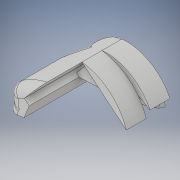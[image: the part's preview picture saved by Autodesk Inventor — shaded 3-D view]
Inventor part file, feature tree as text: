
AUTODESK INVENTOR PART (.ipt)
format: ipt  version: 2017 (Build 210142000, 142)  size: 672,768 bytes
history: native  units: mm
features: sketch x24, extrude x20, fillet x6, plane x5, other x3, boolean_combine x1, revolve x1, sweep x1
ambient origin geometry x8: Origin, YZ Plane, XZ Plane, XY Plane, X Axis, Y Axis, Z Axis, Center Point
bodies: Solid1 (feature_tree), Solid2 (feature_tree), Solid3 (feature_tree), Solid4 (feature_tree), Solid5 (feature_tree)
feature tree (61):
  extrude  "Extrusion1"  Depth=35.0mm
  plane  "Work Plane1"
  extrude  "Extrusion2"  Depth=33.005mm
  extrude  "Extrusion3"  TaperAngle=0.0deg  [1 undecoded]
  plane  "Work Plane2"
  extrude  "Extrusion4"  Depth=20.0mm
  other  "Work Axis1"
  extrude  "Extrusion5"  Depth=10.0mm
  sketch  "Sketch6"  dims[d12=48.556624mm d13=20.0mm d14=0.0mm]
  boolean_combine  "Combine1"
  extrude  "Extrusion6"  Depth=20.0mm TaperAngle=0.0deg
  extrude  "Extrusion7"  Depth=20.0mm TaperAngle=0.0deg
  other  "Work Axis2"
  fillet  "Fillet1"  Radius=53.287466mm
  revolve  "Revolution1"  [1 undecoded]
  extrude  "Extrusion8"  Depth=20.0mm
  sketch  "Sketch10"  dims[d25=7.433428mm d26=13.25mm d27=0.0mm]
  plane  "Work Plane3"
  sweep  "Sweep1"
  extrude  "Extrusion9"  TaperAngle=90.0deg  [1 undecoded]
  fillet  "Fillet2"  Radius=40.197898mm
  extrude  "Extrusion10"  Depth=15.060899mm
  extrude  "Extrusion11"  Depth=10.650813mm
  extrude  "Extrusion12"  Depth=5.3475mm
  fillet  "Fillet3"  Radius=15.0mm
  fillet  "Fillet4"  [1 undecoded]
  fillet  "Fillet5"  Radius=27.295196mm
  other  "Bend Part1"
  extrude  "Extrusion13"  Depth=20.0mm
  plane  "Work Plane4"
  extrude  "Extrusion14"  TaperAngle=0.0deg  [1 undecoded]
  fillet  "Fillet6"  Radius=13.25mm
  extrude  "Extrusion15"  Depth=75.0mm TaperAngle=0.0deg
  plane  "Work Plane5"
  extrude  "Extrusion16"  Depth=10.80569mm
  extrude  "Extrusion17"  Depth=4.8mm TaperAngle=0.0deg
  extrude  "Extrusion18"  Depth=10.0mm
  extrude  "Extrusion19"  Depth=2.0mm TaperAngle=180.0deg
  extrude  "Extrusion20"  Depth=18.153275mm
  sketch  "Sketch1"  dims[d0=60.0mm d1=35.0mm]
  sketch  "Sketch2"  dims[d2=60.0mm d3=33.005mm]
  sketch  "Sketch3"  dims[d4=75.0mm d5=0.0mm d6=0.0mm]
  sketch  "Sketch4"  dims[d7=35.0mm d8=20.0mm]
  sketch  "Sketch5"  dims[d9=55.0mm d10=0.0mm d11=10.0mm]
  sketch  "Sketch7"  dims[d15=90.0deg d16=20.0mm d17=0.0mm d18=53.287466mm]
  sketch  "Sketch8"  dims[d19=20.0mm d20=0.0mm d21=14.476257mm]
  sketch  "Sketch9"  dims[d22=20.0mm d23=0.0mm d24=61.358233mm]
  sketch  "Sketch11"  dims[d28=10.0mm d29=90.0deg d30=40.197898mm]
  sketch  "Sketch12"  dims[d31=90.965929mm d32=15.060899mm]
  sketch  "Sketch13"  dims[d33=0.0mm d34=0.0mm d35=10.650813mm]
  sketch  "Sketch15"  dims[d36=90.0deg d37=5.3475mm d38=15.0mm d39=45.0deg d40=27.295196mm]
  sketch  "Sketch16"  dims[d41=20.0mm d42=5.348mm]
  sketch  "Sketch18"  dims[d43=60.0mm d44=0.0mm d45=0.0mm d46=13.25mm d47=0.0mm]
  sketch  "Sketch19"  dims[d48=10.0mm d49=75.0mm d50=0.0mm]
  sketch  "Sketch20"  dims[d52=10.0mm d53=10.80569mm]
  sketch  "Sketch21"  dims[d54=10.0mm d55=0.0mm d56=4.8mm d57=0.0mm]
  sketch  "Sketch22"  dims[d58=10.0mm d59=10.0mm]
  sketch  "Sketch23"  dims[d60=10.0mm d62=2.0mm d63=180.0deg]
  sketch  "Sketch24"  dims[d64=18.153275mm d65=18.153275mm]
  sketch  "Sketch25"  dims[d66=75.0mm d67=0.0mm]
  sketch  "Sketch26"  dims[d68=90.0deg d69=75.0mm d70=57.396209mm d71=75.0mm d72=0.0mm d73=2.0mm d74=27.7545mm d75=17.5mm d76=5.0mm d77=0.0mm d78=20.0mm d79=28.8585mm d80=10.0mm d81=0.0mm d82=20.0mm d83=3.0mm d85=0.0mm d86=0.0mm d87=10.0mm d88=0.0mm d89=3.357147mm d90=50.0mm d91=0.0mm d92=10.0mm d93=0.0mm d94=19.999532mm d95=2.99993mm d97=13.189012mm d98=19.999532mm d99=2.99993mm d100=0.0mm d101=11.072637mm d102=13.0mm d103=5.0mm d104=0.0mm d105=0.0mm]
note: 5 required parameter values undecoded (feature->parameter linkage not recoverable at this tier; creation-order binding heuristic only, values carry confidence <= 0.55)